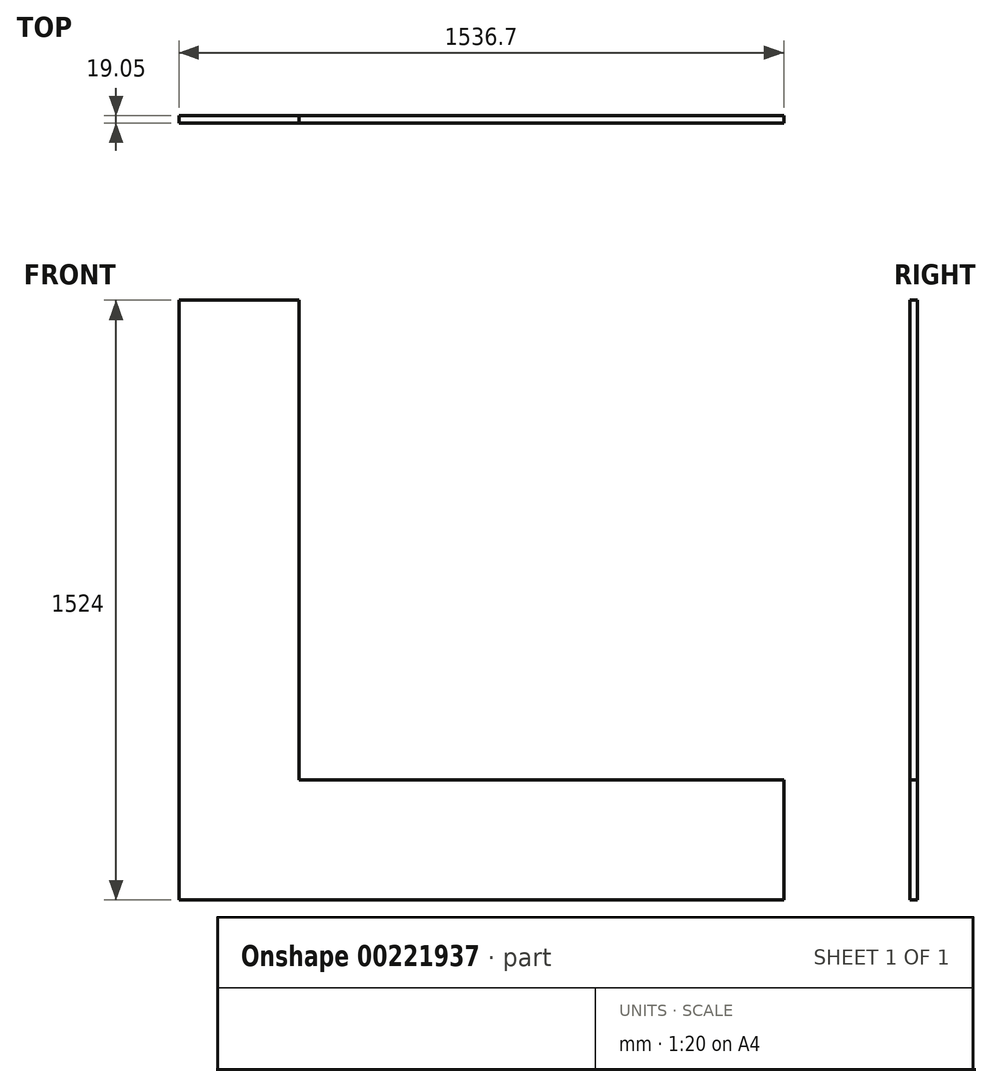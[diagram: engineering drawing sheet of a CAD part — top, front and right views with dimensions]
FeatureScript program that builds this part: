
annotation { "Feature Type Name" : "Feature", "Feature Type Description" : "" }
export const myFeature = defineFeature(function(context is Context, id is Id, definition is map)
    precondition{}
    {
        {
            var Q0;
            Q0=qCreatedBy(makeId("Front.planeOp"),FACE);
            var sketch = newSketch(context, id + "F0", { "sketchPlane" : qUnion([Q0])});
            skLineSegment(sketch, "E0.bottom", {"start": v(-778.2, 861.1) * mm, "end": v(-473.4, 861.1) * mm});
            skLineSegment(sketch, "E0.top", {"start": v(-778.2, -662.9) * mm, "end": v(758.5, -662.9) * mm});
            skLineSegment(sketch, "E0.left", {"start": v(-778.2, 861.1) * mm, "end": v(-778.2, -662.9) * mm});
            skLineSegment(sketch, "E0.right", {"start": v(758.5, -358.1) * mm, "end": v(758.5, -662.9) * mm});
            skLineSegment(sketch, "E1.0", {"start": v(-473.4, 861.1) * mm, "end": v(-473.4, -358.1) * mm});
            skLineSegment(sketch, "E2.0", {"start": v(-473.4, -358.1) * mm, "end": v(758.5, -358.1) * mm});
            skPoint(sketch, "E3.orphan", {"position": v(758.5, 861.1) * mm});
            skSolve(sketch);
        }
        {
            var Q0;
            Q0 = qSketchRegion(id + "F0", true);
            extrude(context, id + "F1", {"entities" : qUnion([Q0]), "depth" : 19.05 * mm});
        }
    });
